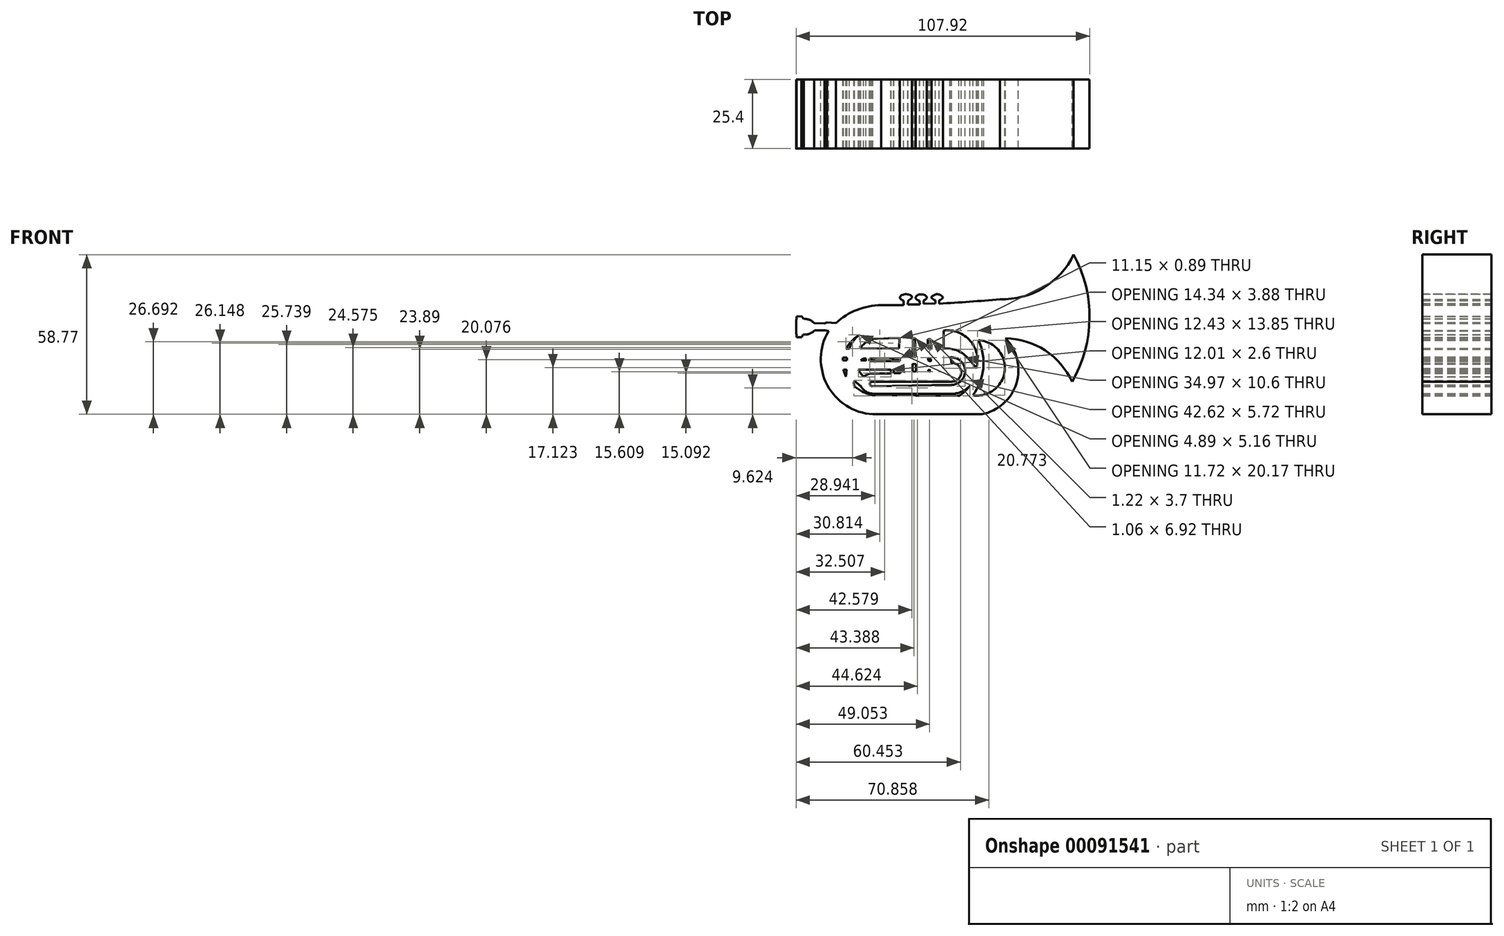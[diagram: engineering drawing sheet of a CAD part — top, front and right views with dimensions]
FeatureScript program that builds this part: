
annotation { "Feature Type Name" : "Feature", "Feature Type Description" : "" }
export const myFeature = defineFeature(function(context is Context, id is Id, definition is map)
    precondition{}
    {
        {
            var Q0;
            Q0=qCreatedBy(makeId("Front.planeOp"),FACE);
            var sketch = newSketch(context, id + "F0", { "sketchPlane" : qUnion([Q0])});
            skPoint(sketch, "E0", {"position": v(-28.94, -8.86) * mm});
            skPoint(sketch, "E1", {"position": v(-22.77, -5.18) * mm});
            skPoint(sketch, "E2", {"position": v(-14.6, -4.98) * mm});
            skPoint(sketch, "E3", {"position": v(-14.7, -8.76) * mm});
            skPoint(sketch, "E4", {"position": v(-25.66, -12.55) * mm});
            skPoint(sketch, "E5", {"position": v(-14.5, -12.35) * mm});
            skPoint(sketch, "E6", {"position": v(-14.5, -13.44) * mm});
            skPoint(sketch, "E7", {"position": v(-25.63, -13.3) * mm});
            skPoint(sketch, "E8", {"position": v(-26.88, -13.3) * mm});
            skPoint(sketch, "E9", {"position": v(-26.88, -12.55) * mm});
            skPoint(sketch, "E10", {"position": v(-28.76, -13.2) * mm});
            skPoint(sketch, "E11", {"position": v(-9.73, -11.91) * mm});
            skPoint(sketch, "E12", {"position": v(-8.67, -11.95) * mm});
            skPoint(sketch, "E13", {"position": v(-9.7, -5.06) * mm});
            skPoint(sketch, "E14", {"position": v(-8.87, -5.04) * mm});
            skPoint(sketch, "E15", {"position": v(-4.15, -5.48) * mm});
            skPoint(sketch, "E16", {"position": v(-3, -5.48) * mm});
            skPoint(sketch, "E17", {"position": v(-4.15, -8.8) * mm});
            skPoint(sketch, "E18", {"position": v(-2.93, -9.18) * mm});
            skPoint(sketch, "E19", {"position": v(-4.04, -12.37) * mm});
            skPoint(sketch, "E20", {"position": v(-3.07, -12.67) * mm});
            skPoint(sketch, "E21", {"position": v(-3.07, -13.64) * mm});
            skPoint(sketch, "E22", {"position": v(-4.11, -13.26) * mm});
            skPoint(sketch, "E23", {"position": v(-4.04, -16.7) * mm});
            skPoint(sketch, "E24", {"position": v(-3.14, -16.92) * mm});
            skPoint(sketch, "E25", {"position": v(-3.67, -17.52) * mm});
            skPoint(sketch, "E26", {"position": v(-9.7, -17.14) * mm});
            skPoint(sketch, "E27", {"position": v(-9.19, -17.37) * mm});
            skPoint(sketch, "E28", {"position": v(-8.55, -17.12) * mm});
            skPoint(sketch, "E29", {"position": v(-8.55, -14.57) * mm});
            skPoint(sketch, "E30", {"position": v(-9.74, -14.51) * mm});
            skPoint(sketch, "E31", {"position": v(-16.75, -16.57) * mm});
            skPoint(sketch, "E32", {"position": v(-14.25, -17.89) * mm});
            skPoint(sketch, "E33", {"position": v(-14.33, -16.6) * mm});
            skPoint(sketch, "E34", {"position": v(-16.65, -17.86) * mm});
            skPoint(sketch, "E35", {"position": v(-16.5, -21.24) * mm});
            skPoint(sketch, "E36", {"position": v(-14.54, -21.08) * mm});
            skPoint(sketch, "E37", {"position": v(-17.73, -16.68) * mm});
            skPoint(sketch, "E38", {"position": v(-29.66, -16.68) * mm});
            skPoint(sketch, "E39", {"position": v(-27.77, -19.28) * mm});
            skPoint(sketch, "E40", {"position": v(-25.14, -18.02) * mm});
            skPoint(sketch, "E41", {"position": v(-17.64, -18.04) * mm});
            skPoint(sketch, "E42", {"position": v(-17.62, -21.1) * mm});
            skPoint(sketch, "E43", {"position": v(-24.88, -21.05) * mm});
            skPoint(sketch, "E44", {"position": v(-24.65, -22.76) * mm});
            skPoint(sketch, "E45", {"position": v(-17.45, -22.69) * mm});
            skPoint(sketch, "E46", {"position": v(-16.41, -22.72) * mm});
            skPoint(sketch, "E47", {"position": v(4.69, -21.04) * mm});
            skPoint(sketch, "E48", {"position": v(4.55, -23.43) * mm});
            skPoint(sketch, "E49", {"position": v(4.4, -14.2) * mm});
            skPoint(sketch, "E50", {"position": v(4, -12.16) * mm});
            skPoint(sketch, "E51", {"position": v(1.72, -5.61) * mm});
            skPoint(sketch, "E52", {"position": v(1.72, -8.89) * mm});
            skPoint(sketch, "E53", {"position": v(10.98, -12.8) * mm});
            skPoint(sketch, "E54", {"position": v(13.69, -16.1) * mm});
            skPoint(sketch, "E55", {"position": v(1.65, -2.27) * mm});
            skPoint(sketch, "E56", {"position": v(14.46, -5.86) * mm});
            skPoint(sketch, "E57", {"position": v(12.4, -26.03) * mm});
            skPoint(sketch, "E58", {"position": v(-35.43, -12) * mm});
            skPoint(sketch, "E59", {"position": v(-35.37, -13.25) * mm});
            skPoint(sketch, "E60", {"position": v(-34.18, -13.25) * mm});
            skPoint(sketch, "E61", {"position": v(-33.95, -12.24) * mm});
            skPoint(sketch, "E62", {"position": v(-35.2, -16.68) * mm});
            skPoint(sketch, "E63", {"position": v(-34.3, -19.22) * mm});
            skPoint(sketch, "E64", {"position": v(-34.07, -16.62) * mm});
            skPoint(sketch, "E65", {"position": v(-31.05, -20.59) * mm});
            skPoint(sketch, "E66", {"position": v(-31.05, -22.84) * mm});
            skPoint(sketch, "E67", {"position": v(-28.8, -22.66) * mm});
            skPoint(sketch, "E68", {"position": v(-24.6, -25.44) * mm});
            skPoint(sketch, "E69", {"position": v(-24.55, -26.03) * mm});
            skPoint(sketch, "E70", {"position": v(7.25, -26.3) * mm});
            skPoint(sketch, "E71", {"position": v(4.54, -25.53) * mm});
            skPoint(sketch, "E72", {"position": v(11.3, -22.64) * mm});
            skPoint(sketch, "E73", {"position": v(24.41, -5.12) * mm});
            skPoint(sketch, "E74", {"position": v(15.76, -31.91) * mm});
            skPoint(sketch, "E75", {"position": v(-24.43, -33.07) * mm});
            skPoint(sketch, "E76", {"position": v(-40.67, -2.48) * mm});
            skPoint(sketch, "E77", {"position": v(-41.94, -2.15) * mm});
            skPoint(sketch, "E78", {"position": v(-45.8, -2.2) * mm});
            skPoint(sketch, "E79", {"position": v(-50, -3.73) * mm});
            skPoint(sketch, "E80", {"position": v(-50.51, -4.76) * mm});
            skPoint(sketch, "E81", {"position": v(-52.4, -4.76) * mm});
            skPoint(sketch, "E82", {"position": v(-52.4, 2.95) * mm});
            skPoint(sketch, "E83", {"position": v(-50.6, 2.99) * mm});
            skPoint(sketch, "E84", {"position": v(-49.8, 2.08) * mm});
            skPoint(sketch, "E85", {"position": v(-45.97, 0.5) * mm});
            skPoint(sketch, "E86", {"position": v(-42.17, 0.42) * mm});
            skPoint(sketch, "E87", {"position": v(-41.23, 0.77) * mm});
            skPoint(sketch, "E88", {"position": v(-37.99, 0.54) * mm});
            skPoint(sketch, "E89", {"position": v(-21.3, 7.14) * mm});
            skPoint(sketch, "E90", {"position": v(-13.01, 7.14) * mm});
            skPoint(sketch, "E91", {"position": v(-13.01, 8.72) * mm});
            skPoint(sketch, "E92", {"position": v(-14.43, 9.75) * mm});
            skPoint(sketch, "E93", {"position": v(-13.4, 10.93) * mm});
            skPoint(sketch, "E94", {"position": v(-10.96, 10.93) * mm});
            skPoint(sketch, "E95", {"position": v(-10, 10.06) * mm});
            skPoint(sketch, "E96", {"position": v(-11.43, 8.8) * mm});
            skPoint(sketch, "E97", {"position": v(-11.5, 7.3) * mm});
            skPoint(sketch, "E98", {"position": v(-7.08, 7.3) * mm});
            skPoint(sketch, "E99", {"position": v(-7.16, 8.72) * mm});
            skPoint(sketch, "E100", {"position": v(-8.66, 9.75) * mm});
            skPoint(sketch, "E101", {"position": v(-7.72, 10.85) * mm});
            skPoint(sketch, "E102", {"position": v(-5.42, 10.85) * mm});
            skPoint(sketch, "E103", {"position": v(-4.56, 9.83) * mm});
            skPoint(sketch, "E104", {"position": v(-5.74, 8.77) * mm});
            skPoint(sketch, "E105", {"position": v(-5.67, 7.58) * mm});
            skPoint(sketch, "E106", {"position": v(-1.45, 7.72) * mm});
            skPoint(sketch, "E107", {"position": v(-1.38, 8.84) * mm});
            skPoint(sketch, "E108", {"position": v(-2.79, 9.9) * mm});
            skPoint(sketch, "E109", {"position": v(-1.66, 10.89) * mm});
            skPoint(sketch, "E110", {"position": v(0, 11.03) * mm});
            skPoint(sketch, "E111", {"position": v(1.37, 9.9) * mm});
            skPoint(sketch, "E112", {"position": v(0, 8.84) * mm});
            skPoint(sketch, "E113", {"position": v(0, 7.65) * mm});
            skPoint(sketch, "E114", {"position": v(22.32, 9.3) * mm});
            skPoint(sketch, "E115", {"position": v(49.47, 25.7) * mm});
            skPoint(sketch, "E116", {"position": v(48.87, -21.14) * mm});
            skPoint(sketch, "E117", {"position": v(55.22, 1.21) * mm});
            skLineSegment(sketch, "E118", {"start": v(-28.94, -8.86) * mm, "end": v(-14.7, -8.76) * mm});
            skLineSegment(sketch, "E119", {"start": v(-14.6, -4.98) * mm, "end": v(-14.7, -8.76) * mm});
            skLineSegment(sketch, "E120", {"start": v(-22.77, -5.18) * mm, "end": v(-14.6, -4.98) * mm});
            skLineSegment(sketch, "E121", {"start": v(-9.7, -5.06) * mm, "end": v(-8.87, -5.04) * mm});
            skLineSegment(sketch, "E122", {"start": v(-8.87, -5.04) * mm, "end": v(-8.67, -11.95) * mm});
            skLineSegment(sketch, "E123", {"start": v(-9.73, -11.91) * mm, "end": v(-8.67, -11.95) * mm});
            skLineSegment(sketch, "E124", {"start": v(-9.7, -5.06) * mm, "end": v(-9.73, -11.91) * mm});
            skLineSegment(sketch, "E125", {"start": v(-28.76, -13.2) * mm, "end": v(-26.88, -13.3) * mm});
            skLineSegment(sketch, "E126", {"start": v(-26.88, -12.55) * mm, "end": v(-26.88, -13.3) * mm});
            skLineSegment(sketch, "E127.bottom", {"start": v(-25.66, -12.55) * mm, "end": v(-14.5, -12.55) * mm});
            skLineSegment(sketch, "E127.top", {"start": v(-25.66, -13.44) * mm, "end": v(-14.5, -13.44) * mm});
            skLineSegment(sketch, "E127.left", {"start": v(-25.66, -12.55) * mm, "end": v(-25.66, -13.44) * mm});
            skLineSegment(sketch, "E127.right", {"start": v(-14.5, -12.55) * mm, "end": v(-14.5, -13.44) * mm});
            skLineSegment(sketch, "E128.bottom", {"start": v(-33.95, -12.24) * mm, "end": v(-35.37, -12.24) * mm});
            skLineSegment(sketch, "E128.top", {"start": v(-33.95, -13.25) * mm, "end": v(-35.37, -13.25) * mm});
            skLineSegment(sketch, "E128.left", {"start": v(-33.95, -12.24) * mm, "end": v(-33.95, -13.25) * mm});
            skLineSegment(sketch, "E128.right", {"start": v(-35.37, -12.24) * mm, "end": v(-35.37, -13.25) * mm});
            skLineSegment(sketch, "E129", {"start": v(-35.2, -16.68) * mm, "end": v(-34.07, -16.62) * mm});
            skLineSegment(sketch, "E130", {"start": v(-34.3, -19.22) * mm, "end": v(-34.07, -16.62) * mm});
            skLineSegment(sketch, "E131", {"start": v(-4.15, -5.48) * mm, "end": v(-3, -5.48) * mm});
            skLineSegment(sketch, "E132", {"start": v(-2.93, -9.18) * mm, "end": v(-3, -5.48) * mm});
            skLineSegment(sketch, "E133", {"start": v(-4.15, -5.48) * mm, "end": v(-4.15, -8.8) * mm});
            skLineSegment(sketch, "E134", {"start": v(-2.93, -9.18) * mm, "end": v(-4.15, -8.8) * mm});
            skLineSegment(sketch, "E135", {"start": v(-4.04, -12.37) * mm, "end": v(-3.07, -12.67) * mm});
            skLineSegment(sketch, "E136", {"start": v(-3.07, -13.64) * mm, "end": v(-3.07, -12.67) * mm});
            skLineSegment(sketch, "E137", {"start": v(-4.04, -12.37) * mm, "end": v(-4.11, -13.26) * mm});
            skLineSegment(sketch, "E138", {"start": v(-4.11, -13.26) * mm, "end": v(-3.07, -13.64) * mm});
            skLineSegment(sketch, "E139", {"start": v(-4.04, -16.7) * mm, "end": v(-3.67, -17.52) * mm});
            skLineSegment(sketch, "E140", {"start": v(-3.14, -16.92) * mm, "end": v(-4.04, -16.7) * mm});
            skLineSegment(sketch, "E141", {"start": v(-3.67, -17.52) * mm, "end": v(-3.14, -16.92) * mm});
            skLineSegment(sketch, "E142", {"start": v(1.72, -5.61) * mm, "end": v(1.72, -8.89) * mm});
            skArc(sketch, "E143", {"start": v(10.98, -12.8) * mm, "mid": v(6.83, -9.7) * mm, "end": v(1.72, -8.89) * mm});
            skArc(sketch, "E144", {"start": v(13.69, -16.1) * mm, "mid": v(12.34, -14.44) * mm, "end": v(10.98, -12.8) * mm});
            skArc(sketch, "E145", {"start": v(13.69, -16.1) * mm, "mid": v(11.37, -5.97) * mm, "end": v(1.65, -2.27) * mm});
            skLineSegment(sketch, "E146", {"start": v(1.65, -2.27) * mm, "end": v(1.72, -5.61) * mm});
            skArc(sketch, "E147", {"start": v(12.4, -26.03) * mm, "mid": v(16.24, -16.23) * mm, "end": v(14.46, -5.86) * mm});
            skArc(sketch, "E148", {"start": v(12.4, -26.03) * mm, "mid": v(24.13, -17.04) * mm, "end": v(14.46, -5.86) * mm});
            skArc(sketch, "E149", {"start": v(-26.88, -12.55) * mm, "mid": v(-27.9, -12.64) * mm, "end": v(-28.76, -13.2) * mm});
            skArc(sketch, "E150", {"start": v(-35.2, -16.68) * mm, "mid": v(-34.81, -17.97) * mm, "end": v(-34.3, -19.22) * mm});
            skArc(sketch, "E151", {"start": v(-29.66, -16.68) * mm, "mid": v(-28.81, -18.05) * mm, "end": v(-27.77, -19.28) * mm});
            skArc(sketch, "E152", {"start": v(-24.88, -21.05) * mm, "mid": v(-25.45, -22) * mm, "end": v(-24.65, -22.76) * mm});
            skArc(sketch, "E153", {"start": v(-28.8, -22.66) * mm, "mid": v(-27.1, -24.66) * mm, "end": v(-24.6, -25.44) * mm});
            skArc(sketch, "E154", {"start": v(-31.05, -22.84) * mm, "mid": v(-28, -24.85) * mm, "end": v(-24.55, -26.03) * mm});
            skArc(sketch, "E155", {"start": v(-31.05, -20.59) * mm, "mid": v(-30.02, -21.73) * mm, "end": v(-28.8, -22.66) * mm});
            skArc(sketch, "E156", {"start": v(-31.05, -20.59) * mm, "mid": v(-31.32, -21.71) * mm, "end": v(-31.05, -22.84) * mm});
            skArc(sketch, "E157", {"start": v(4.69, -21.04) * mm, "mid": v(8.1, -17.47) * mm, "end": v(4.4, -14.2) * mm});
            skArc(sketch, "E158", {"start": v(4.64, -22.25) * mm, "mid": v(9.52, -16.88) * mm, "end": v(4, -12.16) * mm});
            skLineSegment(sketch, "E159", {"start": v(4.64, -22.25) * mm, "end": v(-24.65, -22.76) * mm});
            skLineSegment(sketch, "E160", {"start": v(-24.88, -21.05) * mm, "end": v(4.69, -21.04) * mm});
            skLineSegment(sketch, "E161", {"start": v(-16.75, -16.57) * mm, "end": v(-16.65, -17.86) * mm});
            skLineSegment(sketch, "E162", {"start": v(-16.65, -17.86) * mm, "end": v(-14.25, -17.89) * mm});
            skLineSegment(sketch, "E163", {"start": v(-16.75, -16.57) * mm, "end": v(-14.33, -16.6) * mm});
            skLineSegment(sketch, "E164", {"start": v(-14.25, -17.89) * mm, "end": v(-14.33, -16.6) * mm});
            skLineSegment(sketch, "E165", {"start": v(-9.74, -14.51) * mm, "end": v(-8.55, -14.57) * mm});
            skLineSegment(sketch, "E166", {"start": v(-8.55, -17.12) * mm, "end": v(-8.55, -14.57) * mm});
            skLineSegment(sketch, "E167", {"start": v(-9.19, -17.37) * mm, "end": v(-8.55, -17.12) * mm});
            skLineSegment(sketch, "E168", {"start": v(-9.7, -17.14) * mm, "end": v(-9.19, -17.37) * mm});
            skLineSegment(sketch, "E169", {"start": v(-9.7, -17.14) * mm, "end": v(-9.74, -14.51) * mm});
            skArc(sketch, "E170", {"start": v(-22.77, -5.18) * mm, "mid": v(-26.34, -6.21) * mm, "end": v(-28.94, -8.86) * mm});
            skPoint(sketch, "E171", {"position": v(-34.26, -8.93) * mm});
            skPoint(sketch, "E172", {"position": v(-33.06, -8.96) * mm});
            skPoint(sketch, "E173", {"position": v(-29.37, -3.8) * mm});
            skArc(sketch, "E174", {"start": v(-29.37, -3.8) * mm, "mid": v(-31.55, -6.14) * mm, "end": v(-33.06, -8.96) * mm});
            skArc(sketch, "E175", {"start": v(-29.37, -3.8) * mm, "mid": v(-32.1, -6.1) * mm, "end": v(-34.26, -8.93) * mm});
            skLineSegment(sketch, "E176", {"start": v(-34.26, -8.93) * mm, "end": v(-33.06, -8.96) * mm});
            skLineSegment(sketch, "E177", {"start": v(-24.6, -25.44) * mm, "end": v(4.54, -25.53) * mm});
            skLineSegment(sketch, "E178", {"start": v(-24.55, -26.03) * mm, "end": v(7.25, -26.3) * mm});
            skArc(sketch, "E179", {"start": v(4.54, -25.53) * mm, "mid": v(8.22, -24.78) * mm, "end": v(11.3, -22.64) * mm});
            skArc(sketch, "E180", {"start": v(7.25, -26.3) * mm, "mid": v(9.45, -24.67) * mm, "end": v(11.3, -22.64) * mm});
            skLineSegment(sketch, "E181", {"start": v(-24.43, -33.07) * mm, "end": v(15.76, -33.07) * mm});
            skArc(sketch, "E182", {"start": v(15.76, -33.07) * mm, "mid": v(28.4, -21.67) * mm, "end": v(24.41, -5.12) * mm});
            skArc(sketch, "E183", {"start": v(-40.67, -2.48) * mm, "mid": v(-41.14, -22.34) * mm, "end": v(-24.43, -33.07) * mm});
            skArc(sketch, "E184", {"start": v(-50, -3.73) * mm, "mid": v(-47.73, -3.43) * mm, "end": v(-45.8, -2.2) * mm});
            skArc(sketch, "E185", {"start": v(-45.97, 0.5) * mm, "mid": v(-47.72, 1.7) * mm, "end": v(-49.8, 2.08) * mm});
            skArc(sketch, "E186", {"start": v(-52.4, 2.95) * mm, "mid": v(-52.59, -0.9) * mm, "end": v(-52.4, -4.76) * mm});
            skArc(sketch, "E187", {"start": v(-21.3, 7.14) * mm, "mid": v(-30.24, 5.35) * mm, "end": v(-37.99, 0.54) * mm});
            skArc(sketch, "E188", {"start": v(-21.3, 7.14) * mm, "mid": v(-17.16, 7.12) * mm, "end": v(-13.01, 7.14) * mm});
            skArc(sketch, "E189", {"start": v(22.32, 9.3) * mm, "mid": v(38.35, 13.44) * mm, "end": v(49.47, 25.7) * mm});
            skArc(sketch, "E190", {"start": v(48.87, -21.14) * mm, "mid": v(38.97, -9.57) * mm, "end": v(24.41, -5.12) * mm});
            skArc(sketch, "E191", {"start": v(48.87, -21.14) * mm, "mid": v(55.32, 2.2) * mm, "end": v(49.47, 25.7) * mm});
            skLineSegment(sketch, "E192", {"start": v(-52.4, 2.95) * mm, "end": v(-50.6, 2.99) * mm});
            skLineSegment(sketch, "E193", {"start": v(-50.6, 2.99) * mm, "end": v(-49.8, 2.08) * mm});
            skLineSegment(sketch, "E194", {"start": v(-52.4, -4.76) * mm, "end": v(-50.51, -4.76) * mm});
            skLineSegment(sketch, "E195", {"start": v(-50, -3.73) * mm, "end": v(-50.51, -4.76) * mm});
            skLineSegment(sketch, "E196", {"start": v(-45.8, -2.2) * mm, "end": v(-41.94, -2.15) * mm});
            skLineSegment(sketch, "E197", {"start": v(-41.94, -2.15) * mm, "end": v(-40.67, -2.48) * mm});
            skLineSegment(sketch, "E198", {"start": v(-45.97, 0.5) * mm, "end": v(-42.17, 0.42) * mm});
            skLineSegment(sketch, "E199", {"start": v(-41.23, 0.77) * mm, "end": v(-42.17, 0.42) * mm});
            skLineSegment(sketch, "E200", {"start": v(-41.23, 0.77) * mm, "end": v(-37.99, 0.54) * mm});
            skLineSegment(sketch, "E201", {"start": v(-11.5, 7.3) * mm, "end": v(-7.08, 7.3) * mm});
            skLineSegment(sketch, "E202", {"start": v(-5.67, 7.58) * mm, "end": v(-1.45, 7.72) * mm});
            skArc(sketch, "E203", {"start": v(0, 7.65) * mm, "mid": v(11.17, 8.34) * mm, "end": v(22.32, 9.3) * mm});
            skLineSegment(sketch, "E204", {"start": v(-13.01, 7.14) * mm, "end": v(-13.01, 8.72) * mm});
            skLineSegment(sketch, "E205", {"start": v(-11.5, 7.3) * mm, "end": v(-11.43, 8.8) * mm});
            skLineSegment(sketch, "E206", {"start": v(-7.08, 7.3) * mm, "end": v(-7.16, 8.72) * mm});
            skLineSegment(sketch, "E207", {"start": v(-5.74, 8.77) * mm, "end": v(-5.67, 7.58) * mm});
            skLineSegment(sketch, "E208", {"start": v(-1.45, 7.72) * mm, "end": v(-1.38, 8.84) * mm});
            skLineSegment(sketch, "E209", {"start": v(0, 8.84) * mm, "end": v(0, 7.65) * mm});
            skFitSpline(sketch, "E210", {"points": [v(-13.01, 8.72) * mm, v(-14.43, 9.75) * mm, v(-13.4, 10.93) * mm, v(-10.96, 10.93) * mm, v(-10, 10.06) * mm, v(-11.43, 8.8) * mm, v(-13.01, 8.72) * mm]});
            skFitSpline(sketch, "E211", {"points": [v(-8.66, 9.75) * mm, v(-7.72, 10.85) * mm, v(-5.42, 10.85) * mm, v(-4.56, 9.83) * mm, v(-5.74, 8.77) * mm, v(-7.16, 8.72) * mm, v(-8.66, 9.75) * mm]});
            skFitSpline(sketch, "E212", {"points": [v(-1.38, 8.84) * mm, v(0, 8.84) * mm, v(1.37, 9.9) * mm, v(0, 11.03) * mm, v(-1.66, 10.89) * mm, v(-2.79, 9.9) * mm, v(-1.38, 8.84) * mm]});
            skArc(sketch, "E213", {"start": v(4.4, -14.2) * mm, "mid": v(4.38, -13.15) * mm, "end": v(4, -12.16) * mm});
            skArc(sketch, "E214", {"start": v(-25.14, -18.02) * mm, "mid": v(-26.53, -18.48) * mm, "end": v(-27.77, -19.28) * mm});
            skLineSegment(sketch, "E215", {"start": v(-25.14, -18.02) * mm, "end": v(-17.64, -18.04) * mm});
            skLineSegment(sketch, "E216", {"start": v(-17.64, -18.04) * mm, "end": v(-17.73, -16.68) * mm});
            skLineSegment(sketch, "E217", {"start": v(-17.73, -16.68) * mm, "end": v(-29.66, -16.68) * mm});
            skLineSegment(sketch, "E218", {"start": v(1.72, -5.61) * mm, "end": v(11.28, -5.86) * mm});
            skSolve(sketch);
        }
        {
            var Q0;
            {var subQ0=sQuery(id+"F0.wireOp",EDGE,"E210");var subQ1=makeQuery(id+"F0.imprint","INTERSECT",VERTEX,{"derivedFrom":[sQuery(id+"F0.wireOp",EDGE,"E204"),subQ0]});Q0=makeQuery(id+"F0.imprint","IMPRINT",FACE,{"disambiguationData":[TD([[makeQuery(id+"F0.imprint","IMPRINT",EDGE,{"disambiguationData":[TD([[subQ1,-1.0]])],"derivedFrom":subQ0}),-1.0]])]});}
            var Q1;
            {var subQ0=sQuery(id+"F0.wireOp",EDGE,"E211");var subQ1=makeQuery(id+"F0.imprint","INTERSECT",VERTEX,{"derivedFrom":[sQuery(id+"F0.wireOp",EDGE,"E206"),subQ0]});Q1=makeQuery(id+"F0.imprint","IMPRINT",FACE,{"disambiguationData":[TD([[makeQuery(id+"F0.imprint","IMPRINT",EDGE,{"disambiguationData":[TD([[subQ1,1.0]])],"derivedFrom":subQ0}),-1.0]])]});}
            var Q2;
            {var subQ0=sQuery(id+"F0.wireOp",EDGE,"E212");var subQ1=makeQuery(id+"F0.imprint","INTERSECT",VERTEX,{"derivedFrom":[sQuery(id+"F0.wireOp",EDGE,"E208"),subQ0]});Q2=makeQuery(id+"F0.imprint","IMPRINT",FACE,{"disambiguationData":[TD([[makeQuery(id+"F0.imprint","IMPRINT",EDGE,{"disambiguationData":[TD([[subQ1,-1.0]])],"derivedFrom":subQ0}),1.0]])]});}
            var Q3;
            Q3=makeQuery(id+"F0.imprint","IMPRINT",FACE,{"disambiguationData":[TD([[makeQuery(id+"F0.imprint","IMPRINT",EDGE,{"derivedFrom":sQuery(id+"F0.wireOp",EDGE,"E118")}),-1.0]])]});
            extrude(context, id + "F1", {"entities" : qUnion([Q0, Q1, Q2, Q3]), "depth" : 25.4 * mm});
        }
    });
